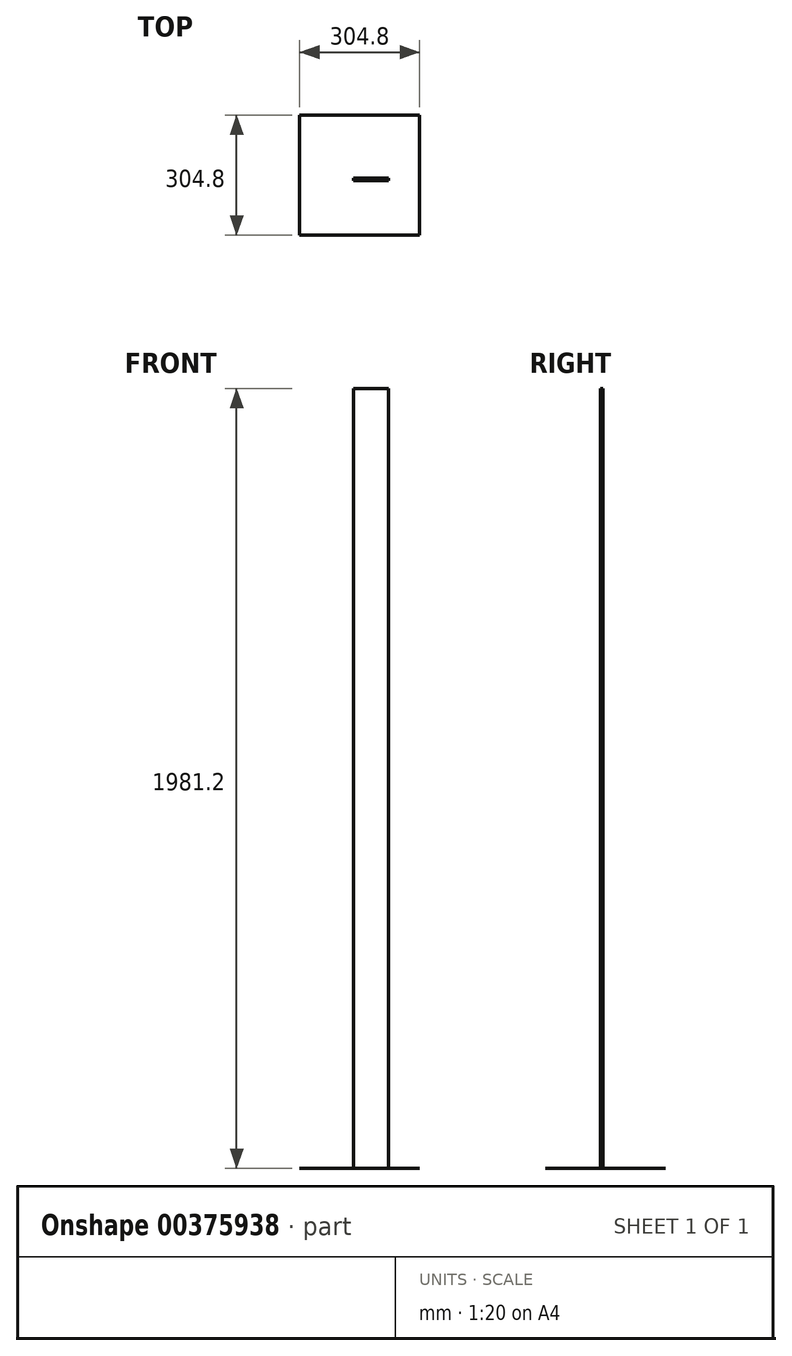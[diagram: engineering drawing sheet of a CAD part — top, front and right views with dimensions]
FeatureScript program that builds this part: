
annotation { "Feature Type Name" : "Feature", "Feature Type Description" : "" }
export const myFeature = defineFeature(function(context is Context, id is Id, definition is map)
    precondition{}
    {
        {
            var Q0;
            Q0=qCreatedBy(makeId("Top.planeOp"),FACE);
            var sketch = newSketch(context, id + "F0", { "sketchPlane" : qUnion([Q0])});
            skLineSegment(sketch, "E0.bottom", {"start": v(-201.33, 156.02) * mm, "end": v(103.47, 156.02) * mm});
            skLineSegment(sketch, "E0.top", {"start": v(-201.33, -148.78) * mm, "end": v(103.47, -148.78) * mm});
            skLineSegment(sketch, "E0.left", {"start": v(-201.33, 156.02) * mm, "end": v(-201.33, -148.78) * mm});
            skLineSegment(sketch, "E0.right", {"start": v(103.47, 156.02) * mm, "end": v(103.47, -148.78) * mm});
            skSolve(sketch);
        }
        {
            var Q0;
            Q0 = qSketchRegion(id + "F0", true);
            extrude(context, id + "F1", {"entities" : qUnion([Q0]), "depth" : 1 / 101.6 * mm});
        }
        {
            var Q0;
            Q0=qCreatedBy(makeId("Top.planeOp"),FACE);
            var sketch = newSketch(context, id + "F2", { "sketchPlane" : qUnion([Q0])});
            skLineSegment(sketch, "E1.bottom", {"start": v(-64.74, -10.12) * mm, "end": v(24.16, -10.12) * mm});
            skLineSegment(sketch, "E1.top", {"start": v(-64.74, -3.77) * mm, "end": v(24.16, -3.77) * mm});
            skLineSegment(sketch, "E1.left", {"start": v(-64.74, -10.12) * mm, "end": v(-64.74, -3.77) * mm});
            skLineSegment(sketch, "E1.right", {"start": v(24.16, -10.12) * mm, "end": v(24.16, -3.77) * mm});
            skSolve(sketch);
        }
        {
            var Q0;
            Q0 = qSketchRegion(id + "F2", true);
            extrude(context, id + "F3", {"entities" : qUnion([Q0]), "operationType" : NewBodyOperationType.ADD, "depth" : 1981.2 * mm});
        }
    });
